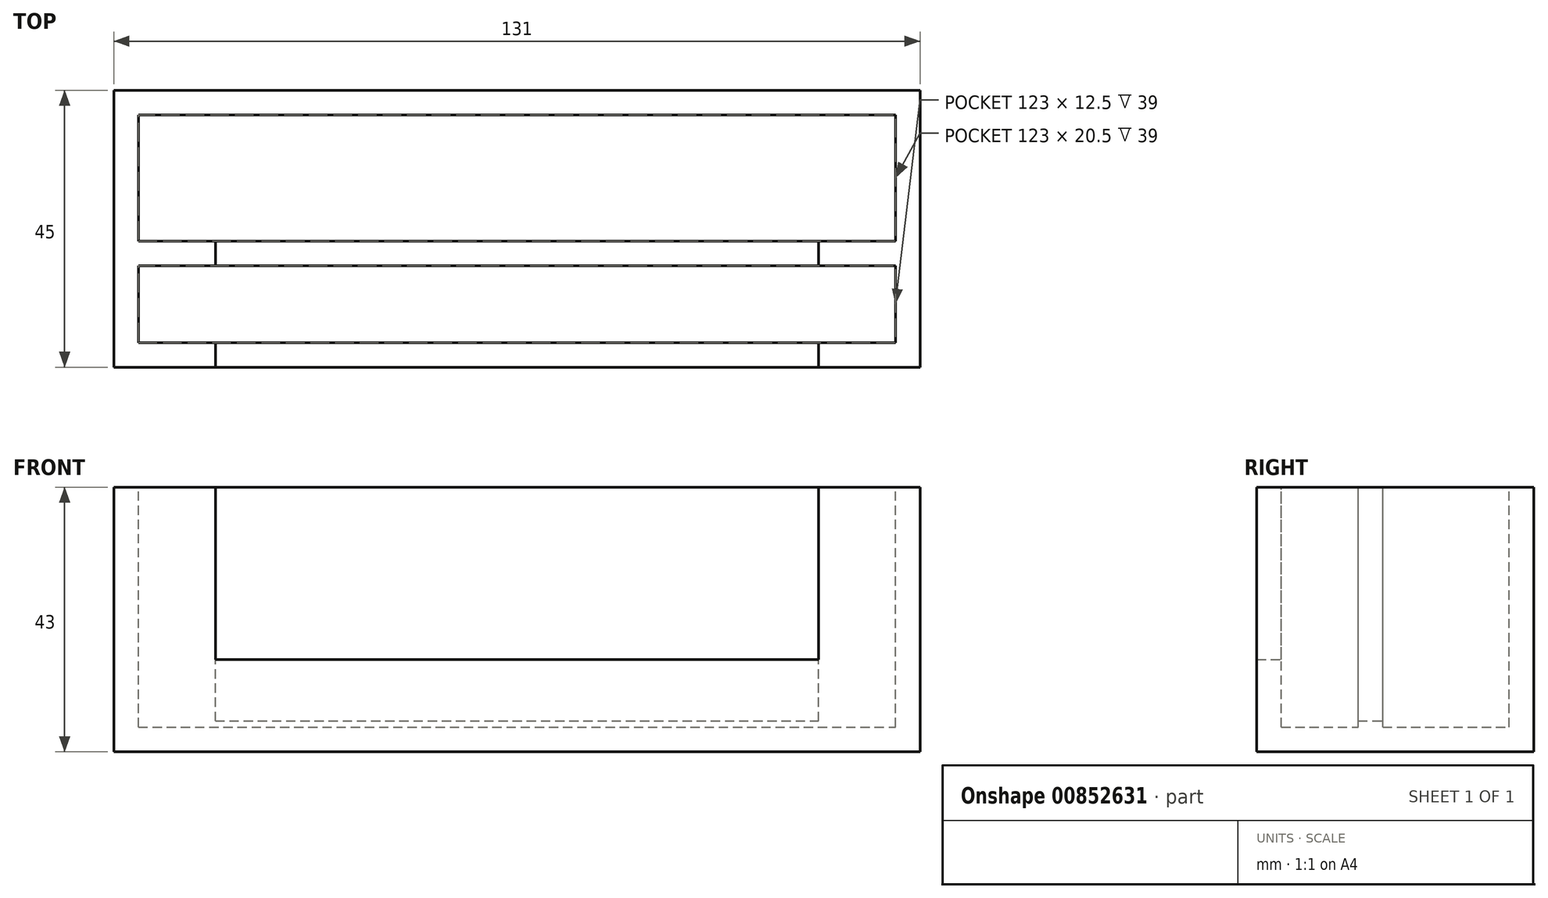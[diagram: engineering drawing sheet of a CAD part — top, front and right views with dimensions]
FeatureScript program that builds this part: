
annotation { "Feature Type Name" : "Feature", "Feature Type Description" : "" }
export const myFeature = defineFeature(function(context is Context, id is Id, definition is map)
    precondition{}
    {
        {
            var Q0;
            Q0=qCreatedBy(makeId("Top.planeOp"),FACE);
            var sketch = newSketch(context, id + "F0", { "sketchPlane" : qUnion([Q0])});
            skLineSegment(sketch, "E0", {"start": v(0, 97.27) * mm, "end": v(0, -104.52) * mm, "construction": true});
            skLineSegment(sketch, "E1", {"start": v(0, 0) * mm, "end": v(-65.5, 0) * mm});
            skLineSegment(sketch, "E2", {"start": v(-65.5, 0) * mm, "end": v(-65.5, 45) * mm});
            skLineSegment(sketch, "E3", {"start": v(-65.5, 45) * mm, "end": v(0, 45) * mm});
            skLineSegment(sketch, "E4.MirrorCS", {"start": v(65.5, 0) * mm, "end": v(65.5, 45) * mm});
            skLineSegment(sketch, "E5.MirrorCS", {"start": v(0, 0) * mm, "end": v(65.5, 0) * mm});
            skLineSegment(sketch, "E6.MirrorCS", {"start": v(65.5, 45) * mm, "end": v(0, 45) * mm});
            skSolve(sketch);
        }
        {
            var Q0;
            Q0 = qSketchRegion(id + "F0", true);
            extrude(context, id + "F1", {"entities" : qUnion([Q0]), "oppositeDirection" : true, "depth" : 43 * mm, "offsetDistance" : 25 * mm});
        }
        {
            var Q0;
            Q0=makeQuery(id+"F1.opExtrude","CAP_FACE",FACE,{"disambiguationData":[OSD([sQuery(id+"F0.wireOp",EDGE,"E1"),sQuery(id+"F0.wireOp",EDGE,"E2"),sQuery(id+"F0.wireOp",EDGE,"E3"),sQuery(id+"F0.wireOp",EDGE,"E4.MirrorCS"),sQuery(id+"F0.wireOp",EDGE,"E5.MirrorCS"),sQuery(id+"F0.wireOp",EDGE,"E6.MirrorCS")])],"isStart":true});
            var sketch = newSketch(context, id + "F2", { "sketchPlane" : qUnion([Q0])});
            skLineSegment(sketch, "E7", {"start": v(0, 0) * mm, "end": v(0, 45) * mm, "construction": true});
            skLineSegment(sketch, "E8", {"start": v(-49, 0) * mm, "end": v(-49, 4) * mm});
            skLineSegment(sketch, "E9", {"start": v(-49, 4) * mm, "end": v(0, 4) * mm});
            skLineSegment(sketch, "E10", {"start": v(-49, 0) * mm, "end": v(0, 0) * mm});
            skLineSegment(sketch, "E11.MirrorCS", {"start": v(49, 0) * mm, "end": v(49, 4) * mm});
            skLineSegment(sketch, "E12.MirrorCS", {"start": v(49, 4) * mm, "end": v(0, 4) * mm});
            skLineSegment(sketch, "E13.MirrorCS", {"start": v(49, 0) * mm, "end": v(0, 0) * mm});
            skSolve(sketch);
        }
        {
            var Q0;
            Q0 = qSketchRegion(id + "F2", true);
            extrude(context, id + "F3", {"entities" : qUnion([Q0]), "operationType" : NewBodyOperationType.REMOVE, "oppositeDirection" : true, "depth" : (56 / 2) * mm, "offsetDistance" : 25 * mm});
        }
        {
            var Q0;
            Q0=makeQuery(id+"F1.opExtrude","CAP_FACE",FACE,{"disambiguationData":[OSD([sQuery(id+"F0.wireOp",EDGE,"E1"),sQuery(id+"F0.wireOp",EDGE,"E2"),sQuery(id+"F0.wireOp",EDGE,"E3"),sQuery(id+"F0.wireOp",EDGE,"E4.MirrorCS"),sQuery(id+"F0.wireOp",EDGE,"E5.MirrorCS"),sQuery(id+"F0.wireOp",EDGE,"E6.MirrorCS")])],"isStart":true});
            var sketch = newSketch(context, id + "F4", { "sketchPlane" : qUnion([Q0])});
            skLineSegment(sketch, "E14.bottom", {"start": v(-61.5, 4) * mm, "end": v(61.5, 4) * mm});
            skLineSegment(sketch, "E14.top", {"start": v(-61.5, 16.5) * mm, "end": v(61.5, 16.5) * mm});
            skLineSegment(sketch, "E14.left", {"start": v(-61.5, 4) * mm, "end": v(-61.5, 16.5) * mm});
            skLineSegment(sketch, "E14.right", {"start": v(61.5, 4) * mm, "end": v(61.5, 16.5) * mm});
            skLineSegment(sketch, "E15", {"start": v(0, 0) * mm, "end": v(0, 45) * mm, "construction": true});
            skSolve(sketch);
        }
        {
            var Q0;
            Q0 = qSketchRegion(id + "F4", true);
            extrude(context, id + "F5", {"entities" : qUnion([Q0]), "operationType" : NewBodyOperationType.REMOVE, "oppositeDirection" : true, "depth" : (78 / 2) * mm, "offsetDistance" : 25 * mm});
        }
        {
            var Q0;
            Q0=makeQuery(id+"F1.opExtrude","CAP_FACE",FACE,{"disambiguationData":[OSD([sQuery(id+"F0.wireOp",EDGE,"E1"),sQuery(id+"F0.wireOp",EDGE,"E2"),sQuery(id+"F0.wireOp",EDGE,"E3"),sQuery(id+"F0.wireOp",EDGE,"E4.MirrorCS"),sQuery(id+"F0.wireOp",EDGE,"E5.MirrorCS"),sQuery(id+"F0.wireOp",EDGE,"E6.MirrorCS")])],"isStart":true});
            var sketch = newSketch(context, id + "F6", { "sketchPlane" : qUnion([Q0])});
            skLineSegment(sketch, "E16.bottom", {"start": v(-49, 16.5) * mm, "end": v(49, 16.5) * mm});
            skLineSegment(sketch, "E16.top", {"start": v(-49, 20.5) * mm, "end": v(49, 20.5) * mm});
            skLineSegment(sketch, "E16.left", {"start": v(-49, 16.5) * mm, "end": v(-49, 20.5) * mm});
            skLineSegment(sketch, "E16.right", {"start": v(49, 16.5) * mm, "end": v(49, 20.5) * mm});
            skSolve(sketch);
        }
        {
            var Q0;
            Q0 = qSketchRegion(id + "F6", true);
            extrude(context, id + "F7", {"entities" : qUnion([Q0]), "operationType" : NewBodyOperationType.REMOVE, "oppositeDirection" : true, "depth" : (42 - 4) * mm, "offsetDistance" : 25 * mm});
        }
        {
            var Q0;
            Q0=makeQuery(id+"F1.opExtrude","CAP_FACE",FACE,{"disambiguationData":[OSD([sQuery(id+"F0.wireOp",EDGE,"E1"),sQuery(id+"F0.wireOp",EDGE,"E2"),sQuery(id+"F0.wireOp",EDGE,"E3"),sQuery(id+"F0.wireOp",EDGE,"E4.MirrorCS"),sQuery(id+"F0.wireOp",EDGE,"E5.MirrorCS"),sQuery(id+"F0.wireOp",EDGE,"E6.MirrorCS")])],"isStart":true});
            var sketch = newSketch(context, id + "F8", { "sketchPlane" : qUnion([Q0])});
            skLineSegment(sketch, "E17.bottom", {"start": v(61.5, 20.5) * mm, "end": v(-61.5, 20.5) * mm});
            skLineSegment(sketch, "E17.top", {"start": v(61.5, 41) * mm, "end": v(-61.5, 41) * mm});
            skLineSegment(sketch, "E17.left", {"start": v(61.5, 20.5) * mm, "end": v(61.5, 41) * mm});
            skLineSegment(sketch, "E17.right", {"start": v(-61.5, 20.5) * mm, "end": v(-61.5, 41) * mm});
            skSolve(sketch);
        }
        {
            var Q0;
            Q0 = qSketchRegion(id + "F8", true);
            extrude(context, id + "F9", {"entities" : qUnion([Q0]), "operationType" : NewBodyOperationType.REMOVE, "oppositeDirection" : true, "depth" : (43 - 4) * mm, "offsetDistance" : 25 * mm});
        }
    });
